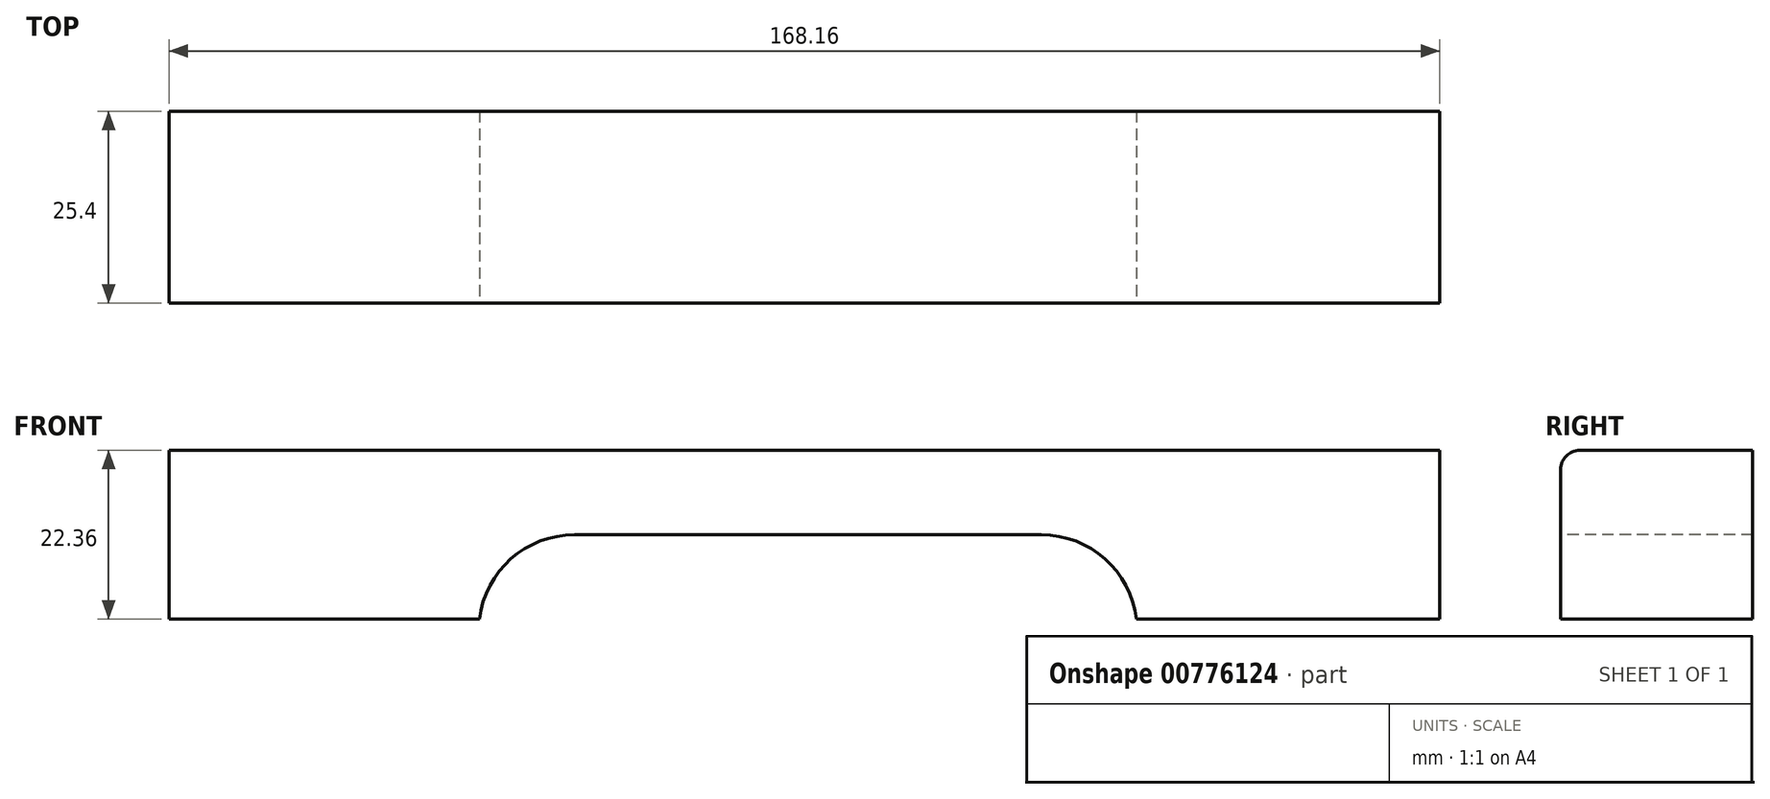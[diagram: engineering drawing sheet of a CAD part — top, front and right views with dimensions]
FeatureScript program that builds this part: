
annotation { "Feature Type Name" : "Feature", "Feature Type Description" : "" }
export const myFeature = defineFeature(function(context is Context, id is Id, definition is map)
    precondition{}
    {
        {
            var Q0;
            Q0=qCreatedBy(makeId("Front.planeOp"),FACE);
            var sketch = newSketch(context, id + "F0", { "sketchPlane" : qUnion([Q0])});
            skLineSegment(sketch, "E0.bottom", {"start": v(84.08, -11.18) * mm, "end": v(-84.08, -11.18) * mm});
            skLineSegment(sketch, "E0.top", {"start": v(84.08, 11.18) * mm, "end": v(-84.08, 11.18) * mm});
            skLineSegment(sketch, "E0.left", {"start": v(84.08, -11.18) * mm, "end": v(84.08, 11.18) * mm});
            skLineSegment(sketch, "E0.right", {"start": v(-84.08, -11.18) * mm, "end": v(-84.08, 11.18) * mm});
            skPoint(sketch, "E0.middle", {"position": v(0, 0) * mm});
            skSolve(sketch);
        }
        {
            var Q0;
            Q0=makeQuery(id+"F0.imprint","IMPRINT",FACE,{"disambiguationData":[TD([[makeQuery(id+"F0.imprint","IMPRINT",EDGE,{"derivedFrom":sQuery(id+"F0.wireOp",EDGE,"E0.bottom")}),-1.0]])]});
            extrude(context, id + "F1", {"entities" : qUnion([Q0]), "depth" : 25.4 * mm, "offsetDistance" : 25.4 * mm});
        }
        {
            var Q0;
            Q0=makeQuery(id+"F1.opExtrude","CAP_FACE",FACE,{"disambiguationData":[OSD([sQuery(id+"F0.wireOp",EDGE,"E0.bottom"),sQuery(id+"F0.wireOp",EDGE,"E0.top"),sQuery(id+"F0.wireOp",EDGE,"E0.left"),sQuery(id+"F0.wireOp",EDGE,"E0.right")])],"isStart":false});
            var sketch = newSketch(context, id + "F2", { "sketchPlane" : qUnion([Q0])});
            skLineSegment(sketch, "E1.bottom", {"start": v(-43.03, -11.18) * mm, "end": v(43.94, -11.18) * mm});
            skLineSegment(sketch, "E1.top", {"start": v(-43.03, 0) * mm, "end": v(43.94, 0) * mm});
            skLineSegment(sketch, "E1.left", {"start": v(-43.03, -11.18) * mm, "end": v(-43.03, 0) * mm});
            skLineSegment(sketch, "E1.right", {"start": v(43.94, -11.18) * mm, "end": v(43.94, 0) * mm});
            skSolve(sketch);
        }
        {
            var Q0;
            Q0 = qSketchRegion(id + "F2", true);
            extrude(context, id + "F3", {"entities" : qUnion([Q0]), "operationType" : NewBodyOperationType.REMOVE, "oppositeDirection" : true, "depth" : 25.4 * mm, "offsetDistance" : 25.4 * mm});
        }
        {
            var Q0;
            Q0=makeQuery(id+"F3.boolean.opBoolean","COPY",EDGE,{"derivedFrom":makeQuery(id+"F3.opExtrude","SWEPT_EDGE",EDGE,{"disambiguationData":[OSD([sQuery(id+"F2.wireOp",EDGE,"E1.top"),sQuery(id+"F2.wireOp",EDGE,"E1.left")])]})});
            fillet(context, id + "F4", {"entities" : qUnion([Q0]), "radius" : 12.7 * mm, "tangentPropagation" : true, "allowEdgeOverflow" : false});
        }
        {
            var Q0;
            Q0=makeQuery(id+"F3.boolean.opBoolean","COPY",EDGE,{"derivedFrom":makeQuery(id+"F3.opExtrude","SWEPT_EDGE",EDGE,{"disambiguationData":[OSD([sQuery(id+"F2.wireOp",EDGE,"E1.top"),sQuery(id+"F2.wireOp",EDGE,"E1.right")])]})});
            fillet(context, id + "F5", {"entities" : qUnion([Q0]), "radius" : 12.7 * mm, "tangentPropagation" : true, "allowEdgeOverflow" : false});
        }
        {
            var Q0;
            Q0=makeQuery(id+"F1.opExtrude","CAP_EDGE",EDGE,{"disambiguationData":[OSD([sQuery(id+"F0.wireOp",EDGE,"E0.top")])],"isStart":false});
            fillet(context, id + "F6", {"entities" : qUnion([Q0]), "radius" : 2.54 * mm, "tangentPropagation" : true, "allowEdgeOverflow" : false});
        }
    });
